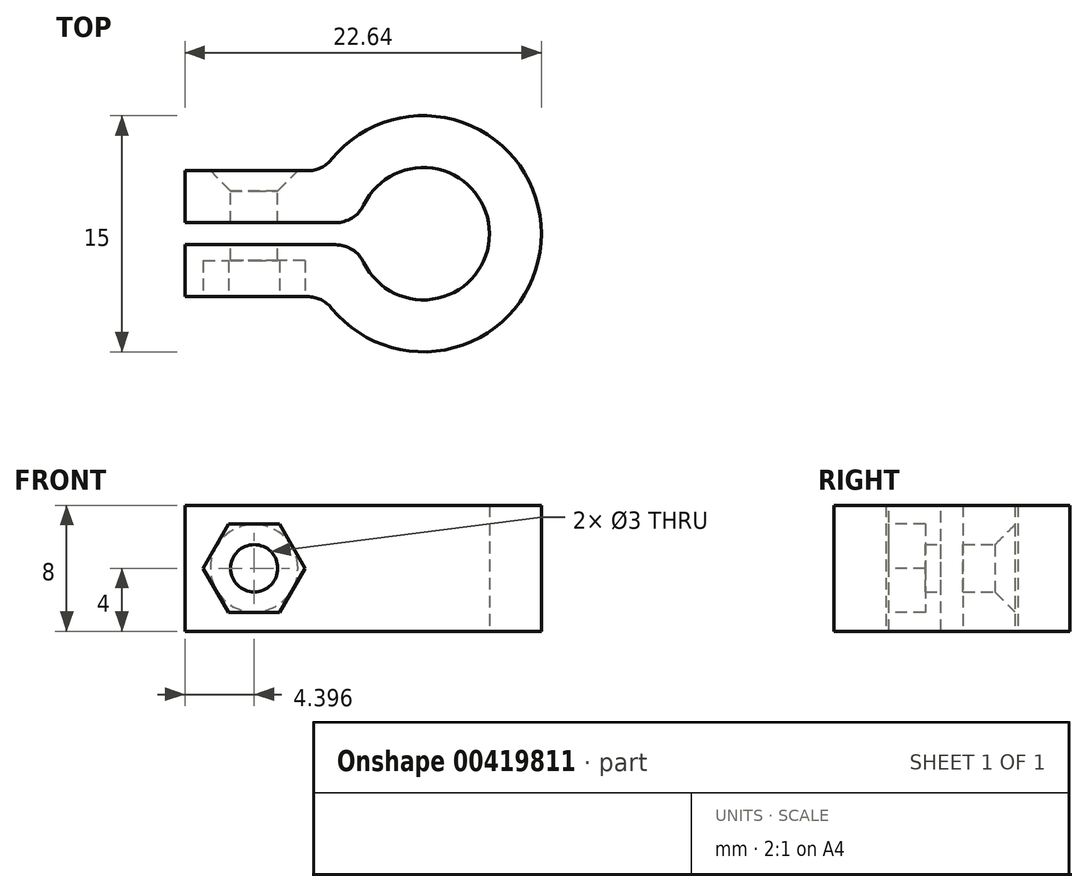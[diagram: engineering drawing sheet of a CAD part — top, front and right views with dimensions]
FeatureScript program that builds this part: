
annotation { "Feature Type Name" : "Feature", "Feature Type Description" : "" }
export const myFeature = defineFeature(function(context is Context, id is Id, definition is map)
    precondition{}
    {
        {
            var Q0;
            Q0=qCreatedBy(makeId("Top.planeOp"),FACE);
            var sketch = newSketch(context, id + "F0", { "sketchPlane" : qUnion([Q0])});
            skArc(sketch, "E0", {"start": v(-4.14, -0.7) * mm, "mid": v(4.2, 0) * mm, "end": v(-4.14, 0.7) * mm});
            skArc(sketch, "E1", {"start": v(-6.34, -4) * mm, "mid": v(7.5, 0) * mm, "end": v(-6.34, 4) * mm});
            skLineSegment(sketch, "E2", {"start": v(-4.14, 0.7) * mm, "end": v(-7.47, 0.7) * mm});
            skLineSegment(sketch, "E3", {"start": v(-7.47, 0.7) * mm, "end": v(-15.14, 0.7) * mm});
            skLineSegment(sketch, "E4.MirrorCS", {"start": v(-7.47, -0.7) * mm, "end": v(-15.14, -0.7) * mm});
            skLineSegment(sketch, "E5.MirrorCS", {"start": v(-4.14, -0.7) * mm, "end": v(-7.47, -0.7) * mm});
            skLineSegment(sketch, "E6", {"start": v(-15.14, 0.7) * mm, "end": v(-15.14, 4) * mm});
            skLineSegment(sketch, "E7", {"start": v(-15.14, 4) * mm, "end": v(-6.34, 4) * mm});
            skLineSegment(sketch, "E8.MirrorCS", {"start": v(-15.14, -0.7) * mm, "end": v(-15.14, -4) * mm});
            skLineSegment(sketch, "E9.MirrorCS", {"start": v(-15.14, -4) * mm, "end": v(-6.34, -4) * mm});
            skLineSegment(sketch, "E10", {"start": v(-6.34, 4) * mm, "end": v(-3.55, 2.24) * mm, "construction": true});
            skLineSegment(sketch, "E11", {"start": v(-6.34, 4) * mm, "end": v(-6.34, 0.7) * mm, "construction": true});
            skLineSegment(sketch, "E12", {"start": v(-15.14, -1.7) * mm, "end": v(-3.84, -1.7) * mm, "construction": true});
            skSolve(sketch);
        }
        {
            var Q0;
            Q0=makeQuery(id+"F0.imprint","IMPRINT",FACE,{"disambiguationData":[TD([[makeQuery(id+"F0.imprint","IMPRINT",EDGE,{"derivedFrom":sQuery(id+"F0.wireOp",EDGE,"E0")}),-1.0]])]});
            extrude(context, id + "F1", {"entities" : qUnion([Q0]), "depth" : 8 * mm});
        }
        {
            var Q0;
            Q0=makeQuery(id+"F1.opExtrude","SWEPT_FACE",FACE,{"disambiguationData":[OSD([sQuery(id+"F0.wireOp",EDGE,"E9.MirrorCS")])]});
            var sketch = newSketch(context, id + "F2", { "sketchPlane" : qUnion([Q0])});
            skLineSegment(sketch, "E13.0.0", {"start": v(-15.14, 0) * mm, "end": v(-6.34, 0) * mm, "construction": true});
            skLineSegment(sketch, "E13.0.1", {"start": v(-6.34, 0) * mm, "end": v(-6.34, 8) * mm, "construction": true});
            skLineSegment(sketch, "E13.0.2", {"start": v(-6.34, 8) * mm, "end": v(-15.14, 8) * mm, "construction": true});
            skLineSegment(sketch, "E13.0.3", {"start": v(-15.14, 8) * mm, "end": v(-15.14, 0) * mm, "construction": true});
            skCircle(sketch, "E14.cCircle", {"center": v(-10.74, 4) * mm, "radius": 2.8 * mm, "construction": true});
            skLineSegment(sketch, "E14.0", {"start": v(-9.13, 1.2) * mm, "end": v(-12.36, 1.2) * mm});
            skLineSegment(sketch, "E14.1", {"start": v(-12.36, 1.2) * mm, "end": v(-13.98, 4) * mm});
            skLineSegment(sketch, "E14.2", {"start": v(-13.98, 4) * mm, "end": v(-12.36, 6.8) * mm});
            skLineSegment(sketch, "E14.3", {"start": v(-12.36, 6.8) * mm, "end": v(-9.13, 6.8) * mm});
            skLineSegment(sketch, "E14.4", {"start": v(-9.13, 6.8) * mm, "end": v(-7.51, 4) * mm});
            skLineSegment(sketch, "E14.5", {"start": v(-7.51, 4) * mm, "end": v(-9.13, 1.2) * mm});
            skPoint(sketch, "E14.0.midPoint", {"position": v(-10.74, 1.2) * mm});
            skLineSegment(sketch, "E15", {"start": v(-15.14, 8) * mm, "end": v(-6.34, 0) * mm, "construction": true});
            skSolve(sketch);
        }
        {
            var Q0;
            Q0=makeQuery(id+"F2.imprint","IMPRINT",FACE,{"disambiguationData":[TD([[makeQuery(id+"F2.imprint","IMPRINT",EDGE,{"derivedFrom":sQuery(id+"F2.wireOp",EDGE,"E14.0")}),-1.0]])]});
            extrude(context, id + "F3", {"entities" : qUnion([Q0]), "operationType" : NewBodyOperationType.REMOVE, "oppositeDirection" : true, "depth" : 2.3 * mm});
        }
        {
            var Q0;
            Q0=makeQuery(id+"F1.opExtrude","SWEPT_FACE",FACE,{"disambiguationData":[OSD([sQuery(id+"F0.wireOp",EDGE,"E7")])]});
            var sketch = newSketch(context, id + "F4", { "sketchPlane" : qUnion([Q0])});
            skLineSegment(sketch, "E16", {"start": v(15.14, 0) * mm, "end": v(6.34, 8) * mm, "construction": true});
            skPoint(sketch, "E17", {"position": v(10.74, 4) * mm});
            skSolve(sketch);
        }
        {
            var Q0;
            Q0=sQuery(id+"F4.wireOp",VERTEX,"E17");
            var Q1;
            Q1=makeQuery(id+"F1.opExtrude","SWEPT_BODY",BODY,{"disambiguationData":[OSD([sQuery(id+"F0.wireOp",EDGE,"E0"),sQuery(id+"F0.wireOp",EDGE,"E1"),sQuery(id+"F0.wireOp",EDGE,"E2"),sQuery(id+"F0.wireOp",EDGE,"E3"),sQuery(id+"F0.wireOp",EDGE,"E4.MirrorCS"),sQuery(id+"F0.wireOp",EDGE,"E5.MirrorCS"),sQuery(id+"F0.wireOp",EDGE,"E6"),sQuery(id+"F0.wireOp",EDGE,"E7"),sQuery(id+"F0.wireOp",EDGE,"E8.MirrorCS"),sQuery(id+"F0.wireOp",EDGE,"E9.MirrorCS")])]});
            hole(context, id + "F5", {"style" : HoleStyle.C_SINK, "endStyle" : HoleEndStyle.THROUGH, "holeDiameter" : 3 * mm, "cSinkDiameter" : 5.55 * mm, "cSinkAngle" : 90 * degree, "isTappedThrough" : true, "tappedDepth" : 12 * mm, "tapClearance" : 3, "locations" : qUnion([Q0]), "scope" : qUnion([Q1])});
        }
        {
            var Q0;
            Q0=makeQuery(id+"F1.opExtrude","SWEPT_EDGE",EDGE,{"disambiguationData":[OSD([sQuery(id+"F0.wireOp",EDGE,"E0"),sQuery(id+"F0.wireOp",EDGE,"E5.MirrorCS")])]});
            var Q1;
            Q1=makeQuery(id+"F1.opExtrude","SWEPT_EDGE",EDGE,{"disambiguationData":[OSD([sQuery(id+"F0.wireOp",EDGE,"E0"),sQuery(id+"F0.wireOp",EDGE,"E2")])]});
            var Q2;
            Q2=makeQuery(id+"F1.opExtrude","SWEPT_EDGE",EDGE,{"disambiguationData":[OSD([sQuery(id+"F0.wireOp",EDGE,"E1"),sQuery(id+"F0.wireOp",EDGE,"E9.MirrorCS")])]});
            var Q3;
            Q3=makeQuery(id+"F1.opExtrude","SWEPT_EDGE",EDGE,{"disambiguationData":[OSD([sQuery(id+"F0.wireOp",EDGE,"E1"),sQuery(id+"F0.wireOp",EDGE,"E7")])]});
            fillet(context, id + "F6", {"entities" : qUnion([Q0, Q1, Q2, Q3]), "radius" : 2 * mm, "tangentPropagation" : true, "allowEdgeOverflow" : false});
        }
    });
